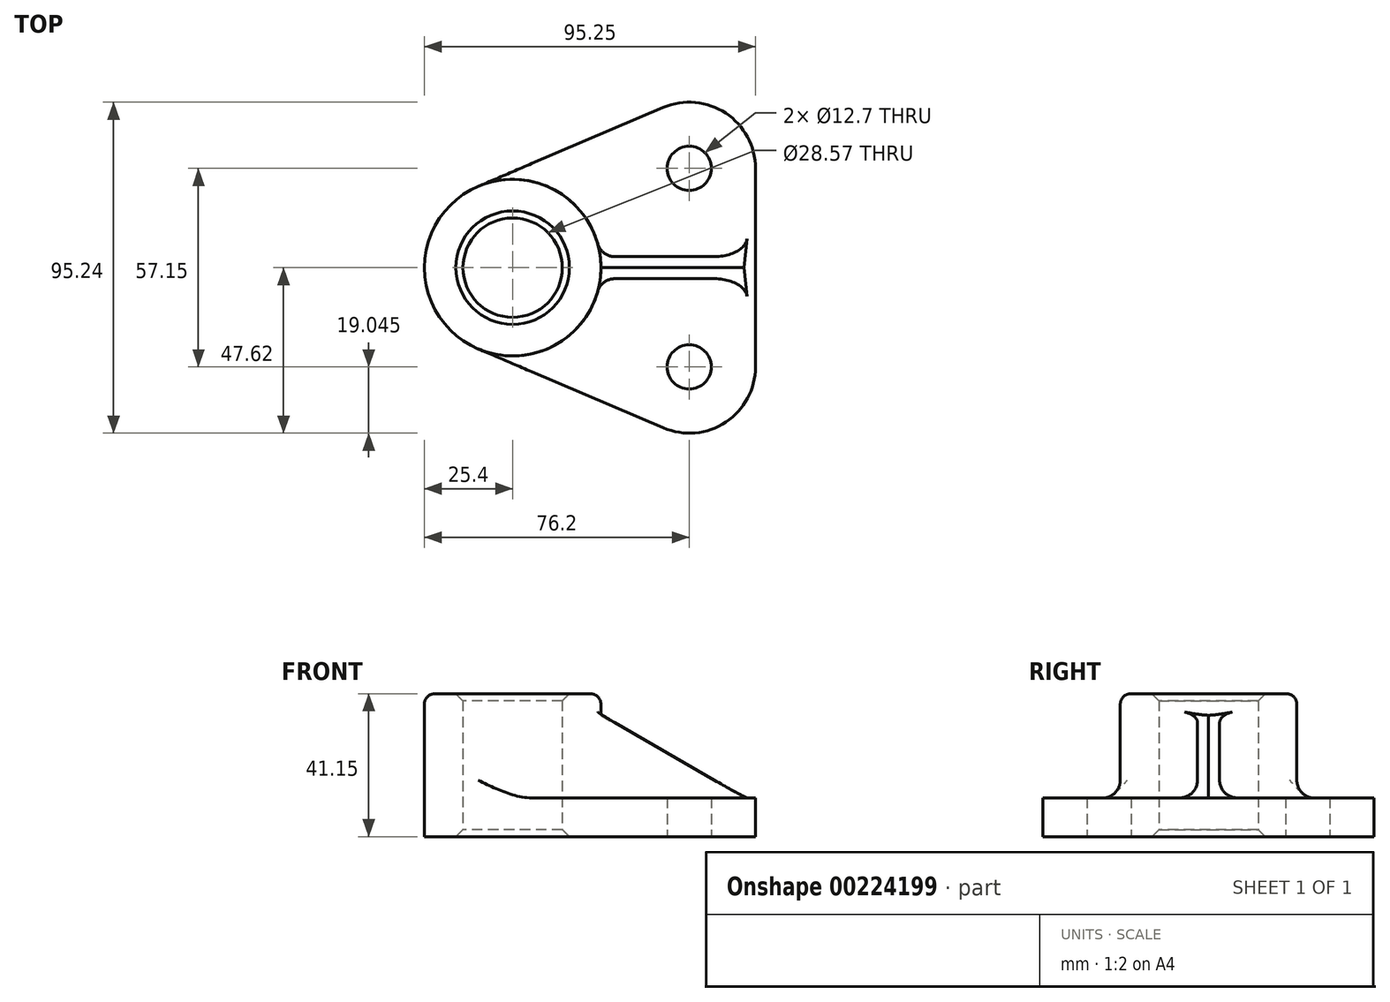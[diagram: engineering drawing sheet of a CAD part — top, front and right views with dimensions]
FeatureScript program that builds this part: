
annotation { "Feature Type Name" : "Feature", "Feature Type Description" : "" }
export const myFeature = defineFeature(function(context is Context, id is Id, definition is map)
    precondition{}
    {
        {
            var Q0;
            Q0=qCreatedBy(makeId("Top.planeOp"),FACE);
            var sketch = newSketch(context, id + "F0", { "sketchPlane" : qUnion([Q0])});
            skCircle(sketch, "E0", {"center": v(0, 0) * mm, "radius": 25.4 * mm});
            skCircle(sketch, "E1", {"center": v(0, 0) * mm, "radius": 14.29 * mm});
            skCircle(sketch, "E2", {"center": v(50.8, 28.58) * mm, "radius": 6.35 * mm});
            skCircle(sketch, "E3", {"center": v(50.8, -28.58) * mm, "radius": 6.35 * mm});
            skLineSegment(sketch, "E4", {"start": v(0, 0) * mm, "end": v(69.85, 0) * mm, "construction": true});
            skArc(sketch, "E5", {"start": v(69.85, 28.58) * mm, "mid": v(61.3, 44.47) * mm, "end": v(43.33, 46.1) * mm});
            skArc(sketch, "E6", {"start": v(43.33, -46.1) * mm, "mid": v(61.3, -44.47) * mm, "end": v(69.85, -28.58) * mm});
            skLineSegment(sketch, "E7", {"start": v(-9.97, -23.36) * mm, "end": v(43.33, -46.1) * mm});
            skLineSegment(sketch, "E8", {"start": v(43.33, 46.1) * mm, "end": v(-9.97, 23.36) * mm});
            skLineSegment(sketch, "E9", {"start": v(69.85, 28.58) * mm, "end": v(69.85, -28.58) * mm});
            skSolve(sketch);
        }
        {
            var Q0;
            Q0=makeQuery(id+"F0.imprint","IMPRINT",FACE,{"disambiguationData":[TD([[makeQuery(id+"F0.imprint","IMPRINT",EDGE,{"derivedFrom":sQuery(id+"F0.wireOp",EDGE,"E1")}),-1.0]])]});
            extrude(context, id + "F1", {"entities" : qUnion([Q0]), "depth" : 41.15 * mm});
        }
        {
            var Q0;
            Q0=makeQuery(id+"F1.opExtrude","CAP_EDGE",EDGE,{"disambiguationData":[OSD([sQuery(id+"F0.wireOp",EDGE,"E0")])],"isStart":false});
            fillet(context, id + "F2", {"entities" : qUnion([Q0]), "radius" : 3.05 * mm, "tangentPropagation" : true, "allowEdgeOverflow" : false});
        }
        {
            var Q0;
            Q0 = qSketchRegion(id + "F0", true);
            extrude(context, id + "F3", {"entities" : qUnion([Q0]), "operationType" : NewBodyOperationType.ADD, "depth" : 11.18 * mm});
        }
        {
            var Q0;
            {var subQ0=sQuery(id+"F0.wireOp",EDGE,"E0");Q0=makeQuery(id+"F3.boolean.opBoolean","INTERSECT",EDGE,{"derivedFrom":[makeQuery(id+"F1.opExtrude","SWEPT_FACE",FACE,{"disambiguationData":[OSD([subQ0])]}),makeQuery(id+"F3.opExtrude","CAP_FACE",FACE,{"disambiguationData":[OSD([subQ0,sQuery(id+"F0.wireOp",EDGE,"E1"),sQuery(id+"F0.wireOp",EDGE,"E2"),sQuery(id+"F0.wireOp",EDGE,"E3"),sQuery(id+"F0.wireOp",EDGE,"E5"),sQuery(id+"F0.wireOp",EDGE,"E6"),sQuery(id+"F0.wireOp",EDGE,"E7"),sQuery(id+"F0.wireOp",EDGE,"E8"),sQuery(id+"F0.wireOp",EDGE,"E9")])],"isStart":false})]});}
            fillet(context, id + "F4", {"entities" : qUnion([Q0]), "radius" : 5.08 * mm, "tangentPropagation" : true, "allowEdgeOverflow" : false});
        }
        {
            var Q0;
            Q0=qCreatedBy(makeId("Front.planeOp"),FACE);
            var sketch = newSketch(context, id + "F5", { "sketchPlane" : qUnion([Q0])});
            skLineSegment(sketch, "E10", {"start": v(25.4, 34.93) * mm, "end": v(25.4, 16.26) * mm});
            skArc(sketch, "E11", {"start": v(25.4, 16.26) * mm, "mid": v(26.89, 12.66) * mm, "end": v(30.48, 11.18) * mm});
            skLineSegment(sketch, "E12.0", {"start": v(30.48, 11.18) * mm, "end": v(43.33, 11.18) * mm});
            skLineSegment(sketch, "E13.0", {"start": v(43.33, 11.18) * mm, "end": v(66.55, 11.18) * mm});
            skLineSegment(sketch, "E14", {"start": v(25.4, 34.93) * mm, "end": v(66.55, 11.18) * mm});
            skSolve(sketch);
        }
        {
            var Q0;
            Q0=makeQuery(id+"F5.imprint","IMPRINT",FACE,{"disambiguationData":[TD([[makeQuery(id+"F5.imprint","IMPRINT",EDGE,{"derivedFrom":sQuery(id+"F5.wireOp",EDGE,"E10")}),1.0]])]});
            extrude(context, id + "F6", {"entities" : qUnion([Q0]), "operationType" : NewBodyOperationType.ADD, "endBound" : BoundingType.SYMMETRIC, "depth" : 6.35 * mm, "hasDraft" : true, "draftAngle" : 3 * degree});
        }
        {
            var Q0;
            Q0=makeQuery(id+"F1.opExtrude","SWEPT_FACE",FACE,{"disambiguationData":[OSD([sQuery(id+"F0.wireOp",EDGE,"E1")])]});
            chamfer(context, id + "F7", {"entities" : qUnion([Q0]), "chamferType" : ChamferType.OFFSET_ANGLE, "width" : 2.03 * mm, "oppositeDirection" : false, "angle" : 45 * degree, "tangentPropagation" : true});
        }
        {
            var Q0;
            Q0=makeQuery(id+"F6.opExtrude","CAP_EDGE",EDGE,{"disambiguationData":[OSD([sQuery(id+"F5.wireOp",EDGE,"E10")])],"isStart":false});
            fillet(context, id + "F8", {"entities" : qUnion([Q0]), "radius" : 12.7 * mm, "tangentPropagation" : true, "allowEdgeOverflow" : false});
        }
        {
            var Q0;
            Q0=makeQuery(id+"F6.boolean.opBoolean","INTERSECT",EDGE,{"derivedFrom":[makeQuery(id+"F3.opExtrude","CAP_FACE",FACE,{"disambiguationData":[OSD([sQuery(id+"F0.wireOp",EDGE,"E0"),sQuery(id+"F0.wireOp",EDGE,"E1"),sQuery(id+"F0.wireOp",EDGE,"E2"),sQuery(id+"F0.wireOp",EDGE,"E3"),sQuery(id+"F0.wireOp",EDGE,"E5"),sQuery(id+"F0.wireOp",EDGE,"E6"),sQuery(id+"F0.wireOp",EDGE,"E7"),sQuery(id+"F0.wireOp",EDGE,"E8"),sQuery(id+"F0.wireOp",EDGE,"E9")])],"isStart":false}),makeQuery(id+"F6.opExtrude","CAP_FACE",FACE,{"disambiguationData":[OSD([sQuery(id+"F5.wireOp",EDGE,"E10"),sQuery(id+"F5.wireOp",EDGE,"E11"),sQuery(id+"F5.wireOp",EDGE,"E12.0"),sQuery(id+"F5.wireOp",EDGE,"E13.0"),sQuery(id+"F5.wireOp",EDGE,"E14")])],"isStart":false})]});
            fillet(context, id + "F9", {"entities" : qUnion([Q0]), "radius" : 5.08 * mm, "tangentPropagation" : true, "allowEdgeOverflow" : false});
        }
        {
            var Q0;
            Q0=makeQuery(id+"F6.opExtrude","CAP_EDGE",EDGE,{"disambiguationData":[OSD([sQuery(id+"F5.wireOp",EDGE,"E10")])],"isStart":true});
            fillet(context, id + "F10", {"entities" : qUnion([Q0]), "radius" : 5.08 * mm, "tangentPropagation" : true, "allowEdgeOverflow" : false});
        }
        {
            var Q0;
            Q0=makeQuery(id+"F6.boolean.opBoolean","INTERSECT",EDGE,{"derivedFrom":[makeQuery(id+"F3.opExtrude","CAP_FACE",FACE,{"disambiguationData":[OSD([sQuery(id+"F0.wireOp",EDGE,"E0"),sQuery(id+"F0.wireOp",EDGE,"E1"),sQuery(id+"F0.wireOp",EDGE,"E2"),sQuery(id+"F0.wireOp",EDGE,"E3"),sQuery(id+"F0.wireOp",EDGE,"E5"),sQuery(id+"F0.wireOp",EDGE,"E6"),sQuery(id+"F0.wireOp",EDGE,"E7"),sQuery(id+"F0.wireOp",EDGE,"E8"),sQuery(id+"F0.wireOp",EDGE,"E9")])],"isStart":false}),makeQuery(id+"F6.opExtrude","CAP_FACE",FACE,{"disambiguationData":[OSD([sQuery(id+"F5.wireOp",EDGE,"E10"),sQuery(id+"F5.wireOp",EDGE,"E11"),sQuery(id+"F5.wireOp",EDGE,"E12.0"),sQuery(id+"F5.wireOp",EDGE,"E13.0"),sQuery(id+"F5.wireOp",EDGE,"E14")])],"isStart":true})]});
            fillet(context, id + "F11", {"entities" : qUnion([Q0]), "radius" : 5.08 * mm, "tangentPropagation" : true, "allowEdgeOverflow" : false});
        }
    });
